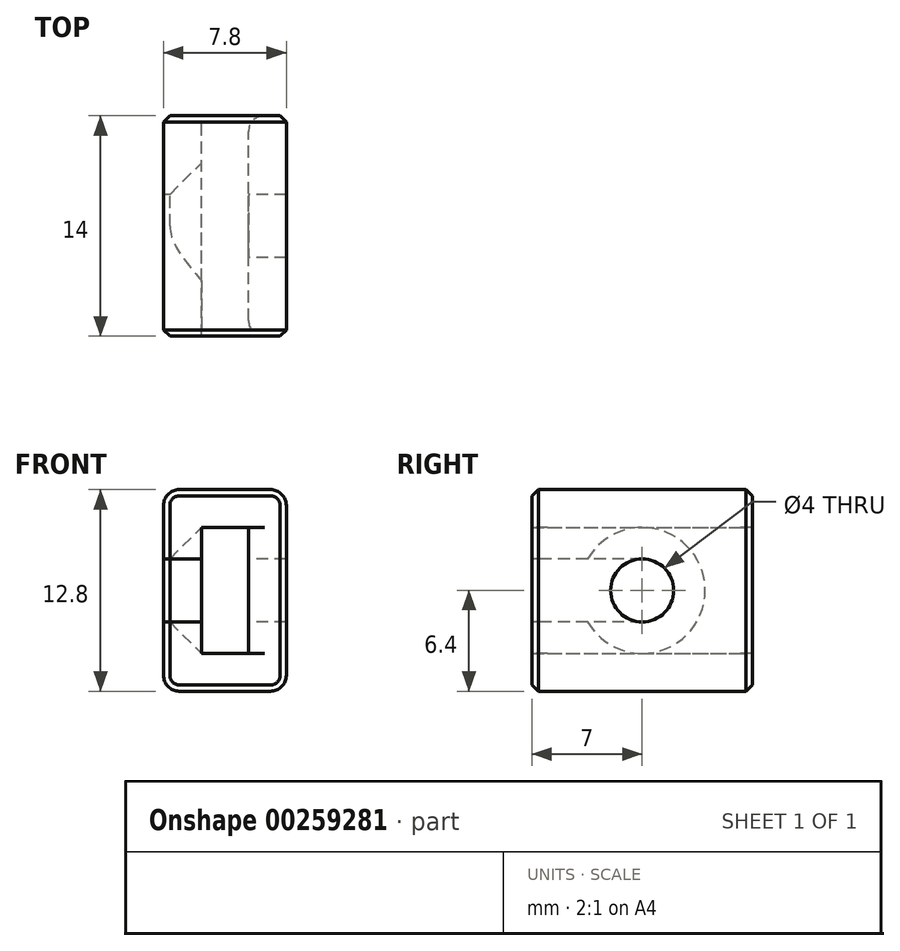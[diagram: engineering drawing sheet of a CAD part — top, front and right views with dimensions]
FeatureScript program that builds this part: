
annotation { "Feature Type Name" : "Feature", "Feature Type Description" : "" }
export const myFeature = defineFeature(function(context is Context, id is Id, definition is map)
    precondition{}
    {
        {
            var Q0;
            Q0=qCreatedBy(makeId("Front.planeOp"),FACE);
            var sketch = newSketch(context, id + "F0", { "sketchPlane" : qUnion([Q0])});
            skLineSegment(sketch, "E0.bottom", {"start": v(-1.5, 4) * mm, "end": v(1.5, 4) * mm});
            skLineSegment(sketch, "E0.top", {"start": v(-1.5, -4) * mm, "end": v(1.5, -4) * mm});
            skLineSegment(sketch, "E0.left", {"start": v(-1.5, 4) * mm, "end": v(-1.5, -4) * mm});
            skLineSegment(sketch, "E0.right", {"start": v(1.5, 4) * mm, "end": v(1.5, -4) * mm});
            skPoint(sketch, "E1", {"position": v(0, 4) * mm});
            skPoint(sketch, "E2", {"position": v(1.5, 0) * mm});
            skLineSegment(sketch, "E3.0", {"start": v(-3.9, 6.4) * mm, "end": v(3.9, 6.4) * mm});
            skLineSegment(sketch, "E3.1", {"start": v(-3.9, 6.4) * mm, "end": v(-3.9, -6.4) * mm});
            skLineSegment(sketch, "E3.2", {"start": v(-3.9, -6.4) * mm, "end": v(3.9, -6.4) * mm});
            skLineSegment(sketch, "E3.3", {"start": v(3.9, 6.4) * mm, "end": v(3.9, -6.4) * mm});
            skSolve(sketch);
        }
        {
            var Q0;
            Q0=makeQuery(id+"F0.imprint","IMPRINT",FACE,{"disambiguationData":[TD([[makeQuery(id+"F0.imprint","IMPRINT",EDGE,{"derivedFrom":sQuery(id+"F0.wireOp",EDGE,"E0.bottom")}),1.0]])]});
            extrude(context, id + "F1", {"entities" : qUnion([Q0]), "depth" : 14 * mm});
        }
        {
            var Q0;
            Q0=makeQuery(id+"F1.opExtrude","SWEPT_FACE",FACE,{"disambiguationData":[OSD([sQuery(id+"F0.wireOp",EDGE,"E3.1")])]});
            var sketch = newSketch(context, id + "F2", { "sketchPlane" : qUnion([Q0])});
            skLineSegment(sketch, "E4", {"start": v(7, -6.4) * mm, "end": v(7, 0) * mm, "construction": true});
            skCircle(sketch, "E5", {"center": v(7, 0) * mm, "radius": 2 * mm});
            skLineSegment(sketch, "E6.bottom", {"start": v(7, 2) * mm, "end": v(14, 2) * mm});
            skLineSegment(sketch, "E6.top", {"start": v(7, -2) * mm, "end": v(14, -2) * mm});
            skLineSegment(sketch, "E6.left", {"start": v(7, 2) * mm, "end": v(7, -2) * mm});
            skLineSegment(sketch, "E6.right", {"start": v(14, 2) * mm, "end": v(14, -2) * mm});
            skSolve(sketch);
        }
        {
            var Q0;
            Q0=makeQuery(id+"F2.imprint","IMPRINT",FACE,{"disambiguationData":[TD([[makeQuery(id+"F2.imprint","IMPRINT",EDGE,{"derivedFrom":sQuery(id+"F2.wireOp",EDGE,"E5")}),1.0]])]});
            var Q1;
            Q1=sQuery(id+"F2.wireOp",EDGE,"E5");
            extrude(context, id + "F3", {"entities" : qUnion([Q0]), "operationType" : NewBodyOperationType.REMOVE, "surfaceEntities" : qUnion([Q1]), "endBound" : BoundingType.THROUGH_ALL, "oppositeDirection" : true, "depth" : 25 * mm});
        }
        {
            var Q0;
            Q0=makeQuery(id+"F3.boolean.opBoolean","INTERSECT",EDGE,{"derivedFrom":[makeQuery(id+"F1.opExtrude","SWEPT_FACE",FACE,{"disambiguationData":[OSD([sQuery(id+"F0.wireOp",EDGE,"E0.left")])]}),makeQuery(id+"F3.opExtrude","SWEPT_FACE",FACE,{"disambiguationData":[OSD([sQuery(id+"F2.wireOp",EDGE,"E5")])]})]});
            chamfer(context, id + "F4", {"entities" : qUnion([Q0]), "width" : 2 * mm, "tangentPropagation" : true});
        }
        {
            var Q0;
            Q0=makeQuery(id+"F1.opExtrude","SWEPT_EDGE",EDGE,{"disambiguationData":[OSD([sQuery(id+"F0.wireOp",EDGE,"E3.0"),sQuery(id+"F0.wireOp",EDGE,"E3.3")])]});
            var Q1;
            Q1=makeQuery(id+"F1.opExtrude","SWEPT_EDGE",EDGE,{"disambiguationData":[OSD([sQuery(id+"F0.wireOp",EDGE,"E3.2"),sQuery(id+"F0.wireOp",EDGE,"E3.3")])]});
            var Q2;
            Q2=makeQuery(id+"F1.opExtrude","SWEPT_EDGE",EDGE,{"disambiguationData":[OSD([sQuery(id+"F0.wireOp",EDGE,"E3.1"),sQuery(id+"F0.wireOp",EDGE,"E3.2")])]});
            var Q3;
            Q3=makeQuery(id+"F1.opExtrude","SWEPT_EDGE",EDGE,{"disambiguationData":[OSD([sQuery(id+"F0.wireOp",EDGE,"E3.0"),sQuery(id+"F0.wireOp",EDGE,"E3.1")])]});
            fillet(context, id + "F5", {"entities" : qUnion([Q0, Q1, Q2, Q3]), "radius" : 1 * mm, "tangentPropagation" : true, "allowEdgeOverflow" : false});
        }
        {
            var Q0;
            Q0=makeQuery(id+"F1.opExtrude","CAP_EDGE",EDGE,{"disambiguationData":[OSD([sQuery(id+"F0.wireOp",EDGE,"E3.3")])],"isStart":false});
            var Q1;
            Q1=makeQuery(id+"F1.opExtrude","CAP_EDGE",EDGE,{"disambiguationData":[OSD([sQuery(id+"F0.wireOp",EDGE,"E3.3")])],"isStart":true});
            chamfer(context, id + "F6", {"entities" : qUnion([Q0, Q1]), "width" : 0.4 * mm, "tangentPropagation" : true});
        }
        {
            var Q0;
            Q0=makeQuery(id+"F1.opExtrude","CAP_EDGE",EDGE,{"disambiguationData":[OSD([sQuery(id+"F0.wireOp",EDGE,"E0.right")])],"isStart":false});
            var Q1;
            Q1=makeQuery(id+"F1.opExtrude","CAP_EDGE",EDGE,{"disambiguationData":[OSD([sQuery(id+"F0.wireOp",EDGE,"E0.right")])],"isStart":true});
            fillet(context, id + "F7", {"entities" : qUnion([Q0, Q1]), "radius" : 1 * mm, "tangentPropagation" : true, "allowEdgeOverflow" : false});
        }
        {
            var Q0;
            {var subQ1=sQuery(id+"F2.wireOp",EDGE,"E6.bottom");Q0=makeQuery(id+"F2.imprint","IMPRINT",FACE,{"disambiguationData":[TD([[makeQuery(id+"F2.imprint","IMPRINT",EDGE,{"derivedFrom":subQ1}),-1.0]])]});}
            extrude(context, id + "F8", {"entities" : qUnion([Q0]), "operationType" : NewBodyOperationType.REMOVE, "endBound" : BoundingType.UP_TO_NEXT, "oppositeDirection" : true, "depth" : 25 * mm});
        }
    });
